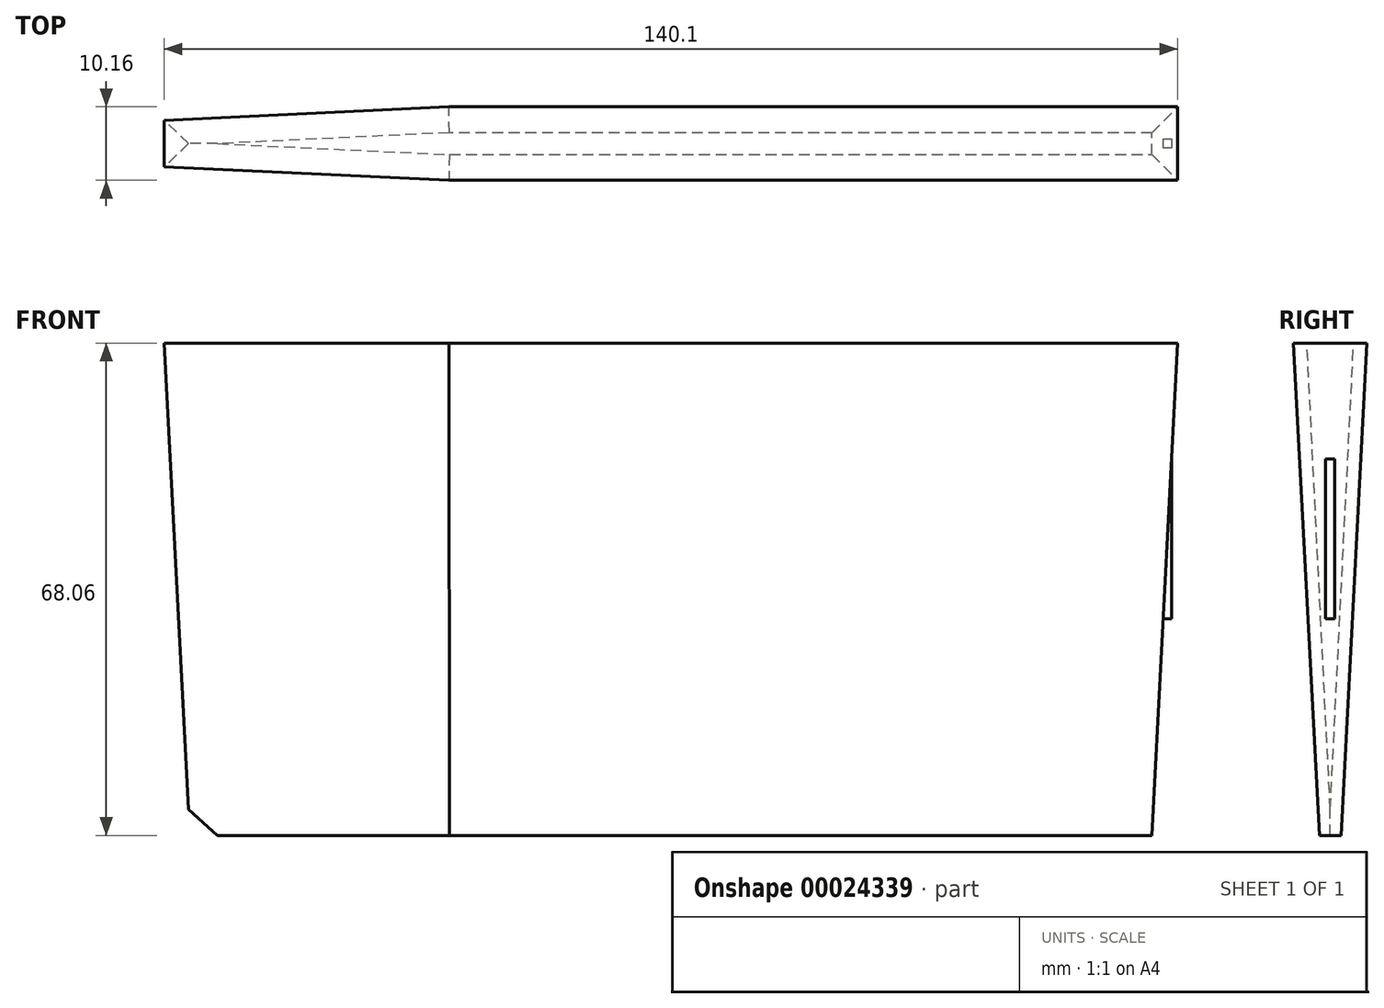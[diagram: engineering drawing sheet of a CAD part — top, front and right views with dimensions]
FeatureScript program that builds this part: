
annotation { "Feature Type Name" : "Feature", "Feature Type Description" : "" }
export const myFeature = defineFeature(function(context is Context, id is Id, definition is map)
    precondition{}
    {
        {
            var Q0;
            Q0=qCreatedBy(makeId("Top.planeOp"),FACE);
            var sketch = newSketch(context, id + "F0", { "sketchPlane" : qUnion([Q0])});
            skLineSegment(sketch, "E0", {"start": v(15.02, 0.63) * mm, "end": v(116.62, 0.63) * mm});
            skLineSegment(sketch, "E1", {"start": v(116.62, 0.63) * mm, "end": v(116.62, -0.64) * mm});
            skLineSegment(sketch, "E2", {"start": v(116.62, -0.64) * mm, "end": v(15.02, -0.64) * mm});
            skArc(sketch, "E3", {"start": v(-13.14, 0) * mm, "mid": v(0.94, -0.48) * mm, "end": v(15.02, -0.63) * mm});
            skArc(sketch, "E4", {"start": v(15.02, 0.63) * mm, "mid": v(0.94, 0.48) * mm, "end": v(-13.14, 0) * mm});
            skLineSegment(sketch, "E5", {"start": v(15.02, 0.63) * mm, "end": v(15.02, -0.63) * mm});
            skLineSegment(sketch, "E6", {"start": v(15.02, 0) * mm, "end": v(-36.85, 0) * mm});
            skSolve(sketch);
        }
        {
            var Q0;
            Q0 = qSketchRegion(id + "F0", true);
            extrude(context, id + "F1", {"entities" : qUnion([Q0]), "oppositeDirection" : true, "depth" : 25.4 * mm});
        }
        {
            var Q0;
            Q0=qCreatedBy(makeId("Top.planeOp"),FACE);
            cPlane(context, id + "F2", {"entities" : qUnion([Q0]), "cplaneType" : CPlaneType.OFFSET, "offset" : 12.7 * mm, "width" : 152.4 * mm, "height" : 152.4 * mm});
        }
        {
            var Q0;
            Q0=qCreatedBy(id+"F2.planeOp",FACE);
            var sketch = newSketch(context, id + "F3", { "sketchPlane" : qUnion([Q0])});
            skLineSegment(sketch, "E7", {"start": v(117.46, 5.08) * mm, "end": v(16.7, 5.08) * mm});
            skLineSegment(sketch, "E8", {"start": v(16.7, 5.08) * mm, "end": v(-22.64, 3.22) * mm});
            skLineSegment(sketch, "E9", {"start": v(-22.64, 3.22) * mm, "end": v(-22.64, -3.22) * mm});
            skLineSegment(sketch, "E10", {"start": v(-22.64, -3.22) * mm, "end": v(16.7, -5.08) * mm});
            skLineSegment(sketch, "E11", {"start": v(16.7, -5.08) * mm, "end": v(117.46, -5.08) * mm});
            skLineSegment(sketch, "E12", {"start": v(117.46, -5.08) * mm, "end": v(117.46, 5.08) * mm});
            skLineSegment(sketch, "E13", {"start": v(16.7, 5.08) * mm, "end": v(16.7, -5.08) * mm});
            skLineSegment(sketch, "E14", {"start": v(-22.64, 0) * mm, "end": v(16.7, 0) * mm});
            skSolve(sketch);
        }
        {
            var Q0;
            {var subQ2=sQuery(id+"F3.wireOp",EDGE,"E7");Q0=makeQuery(id+"F3.imprint","IMPRINT",FACE,{"disambiguationData":[TD([[makeQuery(id+"F3.imprint","IMPRINT",EDGE,{"derivedFrom":subQ2}),1.0]])]});}
            var Q1;
            {var subQ2=sQuery(id+"F3.wireOp",EDGE,"E10");Q1=makeQuery(id+"F3.imprint","IMPRINT",FACE,{"disambiguationData":[TD([[makeQuery(id+"F3.imprint","IMPRINT",EDGE,{"derivedFrom":subQ2}),1.0]])]});}
            var Q2;
            {var subQ2=sQuery(id+"F3.wireOp",EDGE,"E8");Q2=makeQuery(id+"F3.imprint","IMPRINT",FACE,{"disambiguationData":[TD([[makeQuery(id+"F3.imprint","IMPRINT",EDGE,{"derivedFrom":subQ2}),1.0]])]});}
            extrude(context, id + "F4", {"entities" : qUnion([Q0, Q1, Q2]), "operationType" : NewBodyOperationType.ADD, "oppositeDirection" : true, "depth" : 68.06 * mm, "hasDraft" : true, "draftAngle" : 3 * degree, "draftPullDirection" : true});
        }
    });
